# Revit family: Table-Multipurpose-Bernhardt_Design-Revue
name_source: partatom
category: Furniture
revit_build: Autodesk Revit Architecture 2013 (Build: 20130531_2115(x64)
units: mm (PartAtom-declared; Revit-internal decimal feet)

## types (6) — shared parameters
Description = Table
GreenGuard Certification = http://certificates.greenguard.org
Level Certification = http://products.levelcertified.org
Manufacturer = Bernhardt Design
Metal Finish = Metal - Bernhardt Design - Polished Aluminum
Model = See Product Documentation Link to specify exact Model
Product Documentation Link = http://www.bernhardtdesign.com
Product Name = Revue
Product Page URL = http://www.bernhardtdesign.com
Table Finish = Wood - Bernhardt Design - Walnut
Table Height = 2' - 5 1/2"
URL = http://bernhardtdesign.com

## per-type parameters (varying)
| type | Table Depth | Tabletop |
| Round 30 x 30 | 2' - 6" | Tabletop_Round |
| Round 36 x 36 | 3' - 0" | Tabletop_Round |
| Round 42 x 42 | 3' - 6" | Tabletop_Round |
| Square 30 x 30 | 2' - 6" | Tabletop_Square |
| Square 36 x 36 | 3' - 0" | Tabletop_Square |
| Square 42 x 42 | 3' - 6" | Tabletop_Square |

## geometry (parser evidence)
native form markers: Blend x49, Sweep x6
no freeform markers — native parametric forms only
